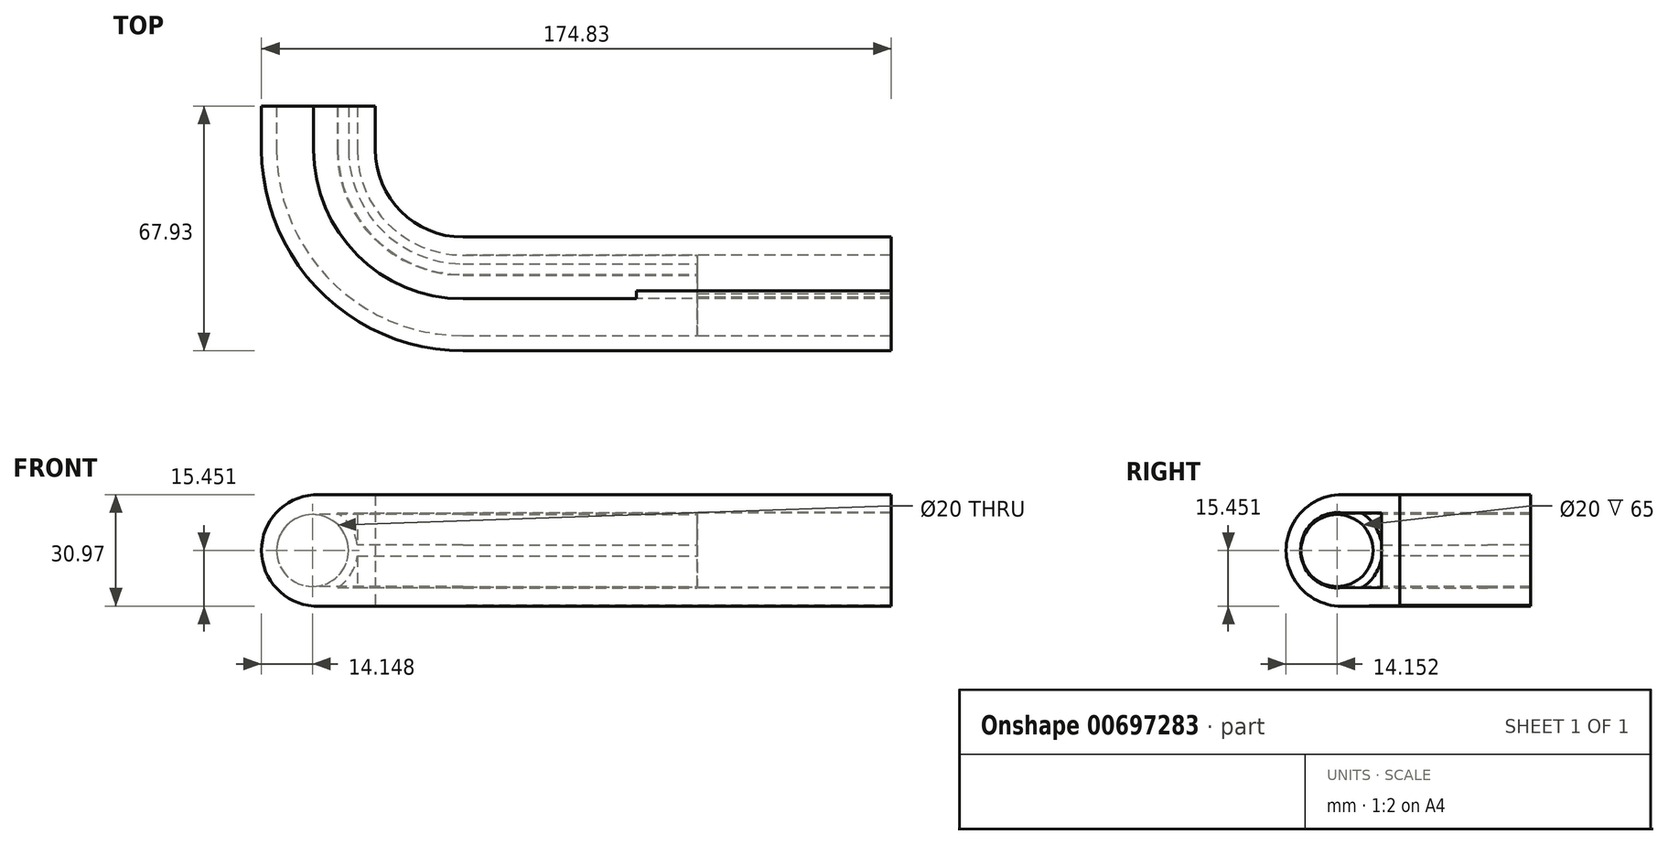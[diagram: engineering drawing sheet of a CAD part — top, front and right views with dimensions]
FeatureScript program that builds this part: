
annotation { "Feature Type Name" : "Feature", "Feature Type Description" : "" }
export const myFeature = defineFeature(function(context is Context, id is Id, definition is map)
    precondition{}
    {
        {
            var Q0;
            Q0=qCreatedBy(makeId("Front.planeOp"),FACE);
            var sketch = newSketch(context, id + "F0", { "sketchPlane" : qUnion([Q0])});
            skCircle(sketch, "E0", {"center": v(-61.98, 30.9) * mm, "radius": 9.5 * mm});
            skCircle(sketch, "E1.0", {"center": v(-61.98, 30.9) * mm, "radius": 12.5 * mm});
            skSolve(sketch);
        }
        {
            var Q0;
            Q0=qCreatedBy(makeId("Top.planeOp"),FACE);
            var sketch = newSketch(context, id + "F1", { "sketchPlane" : qUnion([Q0])});
            skLineSegment(sketch, "E2", {"start": v(-30.2, 0) * mm, "end": v(-30.2, -12) * mm});
            skLineSegment(sketch, "E3", {"start": v(-20.2, -22) * mm, "end": v(44.8, -22) * mm});
            skPoint(sketch, "E4.visualSharp", {"position": v(-30.2, -22) * mm});
            skArc(sketch, "E4.filletArc", {"start": v(-30.2, -12) * mm, "mid": v(-27.27, -19.07) * mm, "end": v(-20.2, -22) * mm});
            skSolve(sketch);
        }
        {
            var Q0;
            Q0=makeQuery(id+"F0.imprint","IMPRINT",FACE,{"disambiguationData":[TD([[makeQuery(id+"F0.imprint","IMPRINT",EDGE,{"derivedFrom":sQuery(id+"F0.wireOp",EDGE,"E0")}),1.0]])]});
            var Q1;
            Q1=makeQuery(id+"F0.imprint","IMPRINT",FACE,{"disambiguationData":[TD([[makeQuery(id+"F0.imprint","IMPRINT",EDGE,{"derivedFrom":sQuery(id+"F0.wireOp",EDGE,"E0")}),-1.0]])]});
            var Q2;
            Q2=sQuery(id+"F1.wireOp",EDGE,"E2");
            var Q3;
            Q3=sQuery(id+"F1.wireOp",EDGE,"E4.filletArc");
            var Q4;
            Q4=sQuery(id+"F1.wireOp",EDGE,"E3");
            sweep(context, id + "F2", {"profiles" : qUnion([Q0, Q1]), "path" : qUnion([Q2, Q3, Q4])});
        }
        {
            var Q0;
            Q0=makeQuery(id+"F2.opSweep","CAP_FACE",FACE,{"disambiguationData":[OSD([sQuery(id+"F0.wireOp",EDGE,"E1.0"),sQuery(id+"F1.wireOp",VERTEX,"E3.end")])],"isStart":false});
            var Q1;
            Q1=makeQuery(id+"F2.opSweep","CAP_FACE",FACE,{"disambiguationData":[OSD([sQuery(id+"F0.wireOp",EDGE,"E1.0"),sQuery(id+"F1.wireOp",VERTEX,"E2.start")])],"isStart":true});
            shell(context, id + "F3", {"entities" : qUnion([Q0, Q1]), "thickness" : 2.5 * mm});
        }
        {
            var Q0;
            Q0=qCreatedBy(makeId("Right.planeOp"),FACE);
            var sketch = newSketch(context, id + "F4", { "sketchPlane" : qUnion([Q0])});
            skArc(sketch, "E5", {"start": v(-52.15, 41.38) * mm, "mid": v(-63.9, 31.43) * mm, "end": v(-53.09, 20.46) * mm});
            skLineSegment(sketch, "E6", {"start": v(-53.4, 20.46) * mm, "end": v(-41.37, 20.64) * mm});
            skLineSegment(sketch, "E7", {"start": v(-54.66, 41.38) * mm, "end": v(-41.37, 41.38) * mm});
            skLineSegment(sketch, "E8", {"start": v(-41.37, 41.38) * mm, "end": v(-41.37, 20.64) * mm});
            skArc(sketch, "E9.trimOffspring", {"start": v(-51.35, 46.38) * mm, "mid": v(-67.9, 31.96) * mm, "end": v(-53.44, 15.45) * mm});
            skLineSegment(sketch, "E10.0", {"start": v(-53.75, 15.45) * mm, "end": v(-36.37, 15.71) * mm});
            skLineSegment(sketch, "E10.1", {"start": v(-36.37, 46.38) * mm, "end": v(-36.37, 15.71) * mm});
            skLineSegment(sketch, "E10.2", {"start": v(-54.12, 46.38) * mm, "end": v(-36.37, 46.38) * mm});
            skSolve(sketch);
        }
        {
            var Q0;
            Q0 = qSketchRegion(id + "F4", true);
            extrude(context, id + "F5", {"entities" : qUnion([Q0]), "operationType" : NewBodyOperationType.ADD, "depth" : 98.7 * mm, "offsetDistance" : 25 * mm, "hasSecondDirection" : true, "secondDirectionOppositeDirection" : false, "secondDirectionDepth" : 27.9 * mm});
        }
        {
            var Q0;
            {var subQ6=sQuery(id+"F4.wireOp",EDGE,"E8");Q0=makeQuery(id+"F4.imprint","IMPRINT",FACE,{"disambiguationData":[TD([[makeQuery(id+"F4.imprint","IMPRINT",EDGE,{"derivedFrom":subQ6}),1.0]])]});}
            var Q1;
            Q1 = qConstructionFilter(qBodyType(qCreatedBy(id + "F1" ,EDGE), BodyType.WIRE), ConstructionObject.NO);
            sweep(context, id + "F6", {"operationType" : NewBodyOperationType.ADD, "profiles" : qUnion([Q0]), "path" : qUnion([Q1])});
        }
    });
